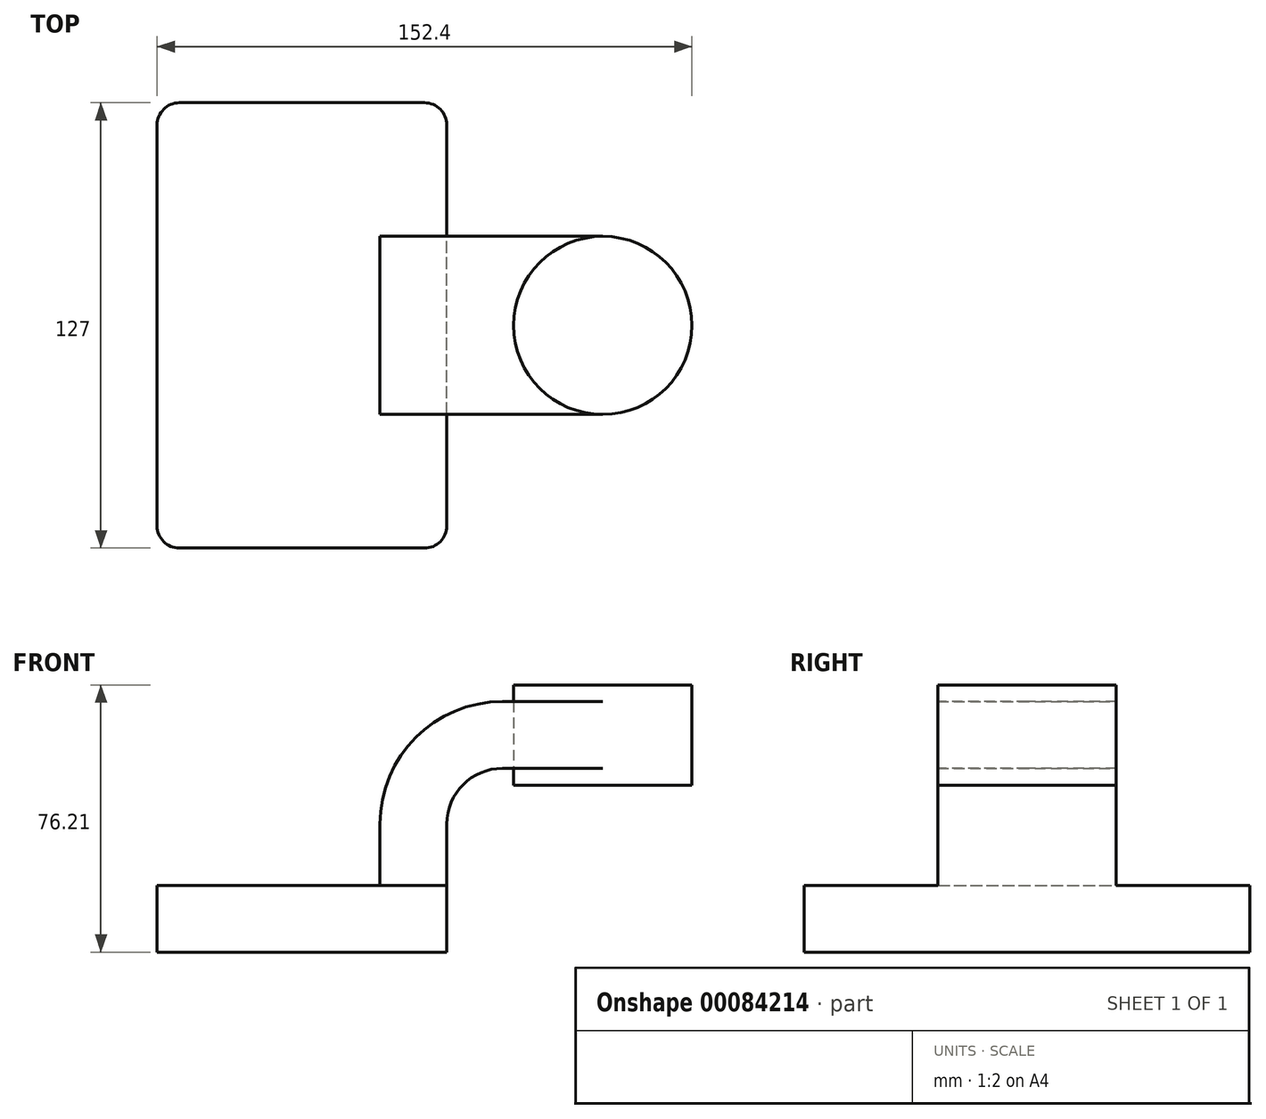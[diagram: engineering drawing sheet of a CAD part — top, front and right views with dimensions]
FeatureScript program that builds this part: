
annotation { "Feature Type Name" : "Feature", "Feature Type Description" : "" }
export const myFeature = defineFeature(function(context is Context, id is Id, definition is map)
    precondition{}
    {
        {
            var Q0;
            Q0=qCreatedBy(makeId("Front.planeOp"),FACE);
            var sketch = newSketch(context, id + "F0", { "sketchPlane" : qUnion([Q0])});
            skLineSegment(sketch, "E0.bottom", {"start": v(-41.28, -9.53) * mm, "end": v(41.28, -9.53) * mm});
            skLineSegment(sketch, "E0.top", {"start": v(-41.28, 9.52) * mm, "end": v(41.28, 9.52) * mm});
            skLineSegment(sketch, "E0.left", {"start": v(-41.27, -9.53) * mm, "end": v(-41.28, 9.52) * mm});
            skLineSegment(sketch, "E0.right", {"start": v(41.28, -9.53) * mm, "end": v(41.28, 9.52) * mm});
            skPoint(sketch, "E0.middle", {"position": v(0, 0) * mm});
            skLineSegment(sketch, "E1.bottom", {"start": v(60.32, 38.1) * mm, "end": v(111.12, 38.1) * mm});
            skLineSegment(sketch, "E1.top", {"start": v(60.32, 66.67) * mm, "end": v(111.12, 66.67) * mm});
            skLineSegment(sketch, "E1.left", {"start": v(60.32, 38.1) * mm, "end": v(60.32, 66.67) * mm});
            skLineSegment(sketch, "E1.right", {"start": v(111.12, 38.1) * mm, "end": v(111.12, 66.67) * mm});
            skPoint(sketch, "E1.middle", {"position": v(85.72, 52.39) * mm});
            skLineSegment(sketch, "E2", {"start": v(41.27, 9.52) * mm, "end": v(41.27, 27) * mm});
            skArc(sketch, "E3", {"start": v(41.27, 27) * mm, "mid": v(45.92, 38.23) * mm, "end": v(57.15, 42.88) * mm});
            skLineSegment(sketch, "E4", {"start": v(57.15, 42.88) * mm, "end": v(85.72, 42.88) * mm});
            skLineSegment(sketch, "E5.0", {"start": v(57.15, 61.93) * mm, "end": v(85.72, 61.93) * mm});
            skArc(sketch, "E5.1", {"start": v(22.22, 27) * mm, "mid": v(32.45, 51.7) * mm, "end": v(57.15, 61.93) * mm});
            skLineSegment(sketch, "E5.2", {"start": v(22.22, 9.52) * mm, "end": v(22.22, 27) * mm});
            skLineSegment(sketch, "E6", {"start": v(85.72, 38.1) * mm, "end": v(85.72, 66.67) * mm});
            skFitSpline(sketch, "E7", {"points": [v(-41.28, 9.53) * mm, v(57.15, 61.93) * mm], "startDerivative": vector(24.22, 138.05) * mm, "endDerivative": vector(128.76, 0) * mm});
            skSolve(sketch);
        }
        {
            var Q0;
            Q0=makeQuery(id+"F0.imprint","IMPRINT",FACE,{"disambiguationData":[TD([[makeQuery(id+"F0.imprint","IMPRINT",EDGE,{"derivedFrom":sQuery(id+"F0.wireOp",EDGE,"E0.bottom")}),1.0]])]});
            extrude(context, id + "F1", {"entities" : qUnion([Q0]), "depth" : 127 * mm, "symmetric" : true});
        }
        {
            var Q0;
            {var subQ1=sQuery(id+"F0.wireOp",EDGE,"E2");Q0=makeQuery(id+"F0.imprint","IMPRINT",FACE,{"disambiguationData":[TD([[makeQuery(id+"F0.imprint","IMPRINT",EDGE,{"derivedFrom":subQ1}),1.0]])]});}
            var Q1;
            {var subQ0=sQuery(id+"F0.wireOp",EDGE,"E4");var subQ1=sQuery(id+"F0.wireOp",EDGE,"E1.left");var subQ2=makeQuery(id+"F0.imprint","INTERSECT",VERTEX,{"derivedFrom":[subQ1,subQ0]});Q1=makeQuery(id+"F0.imprint","IMPRINT",FACE,{"disambiguationData":[TD([[makeQuery(id+"F0.imprint","IMPRINT",EDGE,{"disambiguationData":[TD([[subQ2,-1.0]])],"derivedFrom":subQ1}),-1.0]])]});}
            extrude(context, id + "F2", {"entities" : qUnion([Q0, Q1]), "operationType" : NewBodyOperationType.ADD, "depth" : 50.8 * mm, "symmetric" : true});
        }
        {
            var Q0;
            Q0=makeQuery(id+"F0.imprint","IMPRINT",FACE,{"disambiguationData":[TD([[makeQuery(id+"F0.imprint","IMPRINT",EDGE,{"derivedFrom":sQuery(id+"F0.wireOp",EDGE,"E5.1")}),1.0]])]});
            extrude(context, id + "F3", {"entities" : qUnion([Q0]), "operationType" : NewBodyOperationType.ADD, "depth" : 15.88 * mm});
        }
        {
            var Q0;
            {var subQ0=sQuery(id+"F0.wireOp",EDGE,"E1.right");Q0=makeQuery(id+"F0.imprint","IMPRINT",FACE,{"disambiguationData":[TD([[makeQuery(id+"F0.imprint","IMPRINT",EDGE,{"derivedFrom":subQ0}),1.0]])]});}
            var Q1;
            Q1=sQuery(id+"F0.wireOp",EDGE,"E6");
            revolve(context, id + "F4", {"entities" : qUnion([Q0]), "axis" : qUnion([Q1]), "revolveType" : RevolveType.FULL});
        }
        {
            var Q0;
            Q0=makeQuery(id+"F1.opExtrude","CAP_EDGE",EDGE,{"disambiguationData":[OSD([sQuery(id+"F0.wireOp",EDGE,"E0.right")])],"isStart":false});
            var Q1;
            Q1=makeQuery(id+"F1.opExtrude","CAP_EDGE",EDGE,{"disambiguationData":[OSD([sQuery(id+"F0.wireOp",EDGE,"E0.left")])],"isStart":false});
            var Q2;
            Q2=makeQuery(id+"F1.opExtrude","CAP_EDGE",EDGE,{"disambiguationData":[OSD([sQuery(id+"F0.wireOp",EDGE,"E0.right")])],"isStart":true});
            var Q3;
            Q3=makeQuery(id+"F1.opExtrude","CAP_EDGE",EDGE,{"disambiguationData":[OSD([sQuery(id+"F0.wireOp",EDGE,"E0.left")])],"isStart":true});
            fillet(context, id + "F5", {"entities" : qUnion([Q0, Q1, Q2, Q3]), "radius" : 6.35 * mm, "tangentPropagation" : true, "allowEdgeOverflow" : false});
        }
    });
